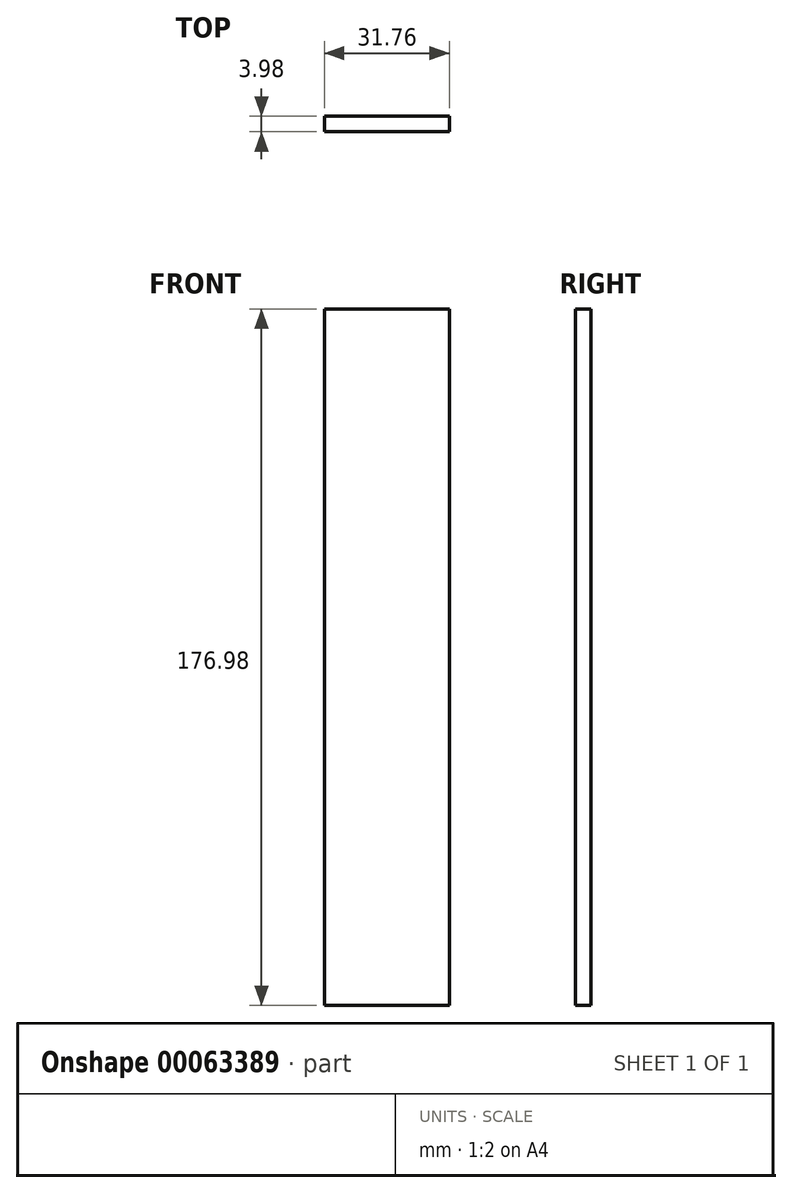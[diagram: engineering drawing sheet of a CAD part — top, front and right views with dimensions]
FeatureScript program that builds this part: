
annotation { "Feature Type Name" : "Feature", "Feature Type Description" : "" }
export const myFeature = defineFeature(function(context is Context, id is Id, definition is map)
    precondition{}
    {
        {
            var Q0;
            Q0=qCreatedBy(makeId("Top.planeOp"),FACE);
            var sketch = newSketch(context, id + "F0", { "sketchPlane" : qUnion([Q0])});
            skLineSegment(sketch, "E0.rect.bottom", {"start": v(15.87, 2) * mm, "end": v(-15.88, 2) * mm});
            skLineSegment(sketch, "E0.rect.top", {"start": v(15.87, -2) * mm, "end": v(-15.88, -2) * mm});
            skLineSegment(sketch, "E0.rect.left", {"start": v(15.87, 2) * mm, "end": v(15.87, -2) * mm});
            skLineSegment(sketch, "E0.rect.right", {"start": v(-15.88, 2) * mm, "end": v(-15.88, -2) * mm});
            skPoint(sketch, "E0.rect.middle", {"position": v(0, 0) * mm});
            skSolve(sketch);
        }
        {
            var Q0;
            Q0=qSketchRegion(id+"F0",true);
            extrude(context, id + "F1", {"entities" : qUnion([Q0]), "endBound" : BoundingType.SYMMETRIC, "depth" : 176.98 * mm});
        }
    });
